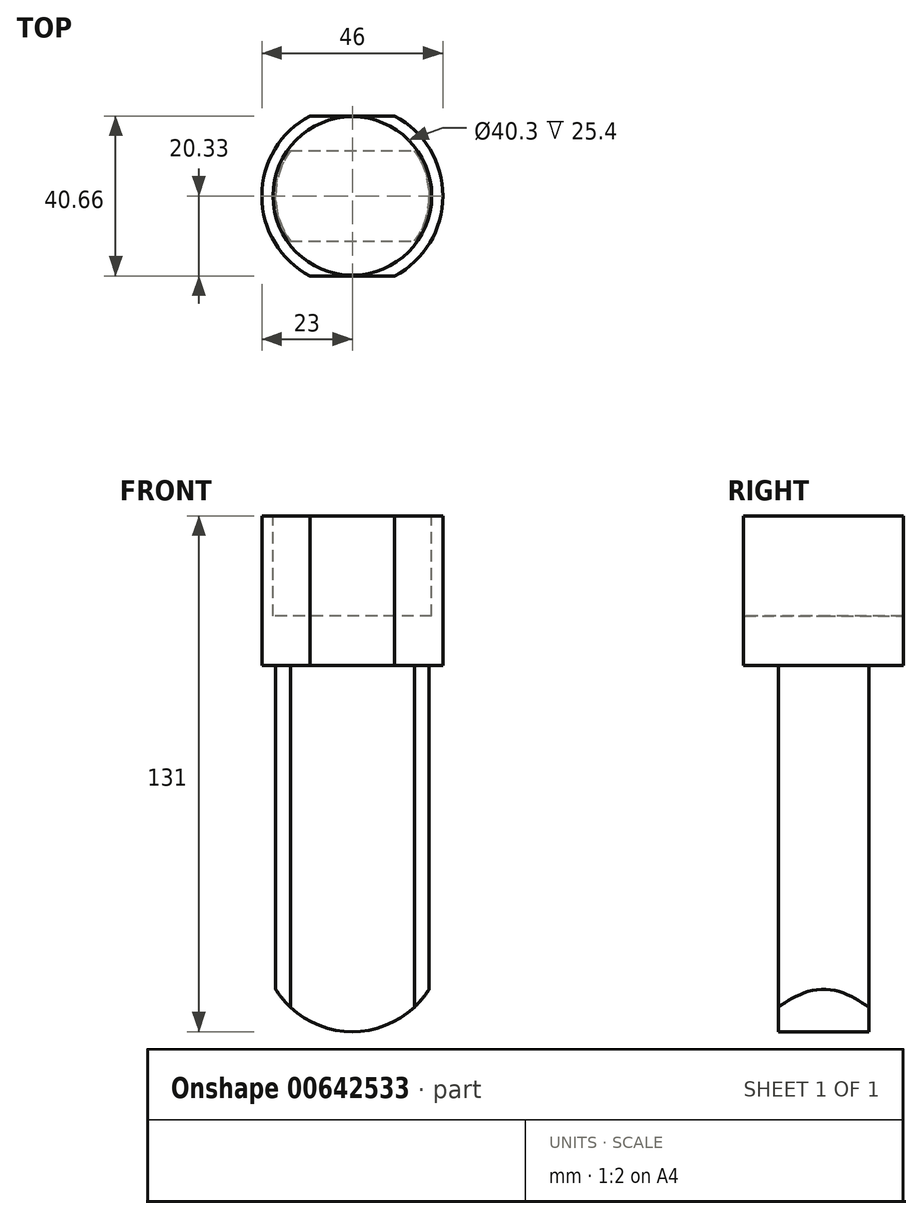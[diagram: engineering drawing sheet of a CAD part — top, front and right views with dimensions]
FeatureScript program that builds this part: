
annotation { "Feature Type Name" : "Feature", "Feature Type Description" : "" }
export const myFeature = defineFeature(function(context is Context, id is Id, definition is map)
    precondition{}
    {
        {
            var Q0;
            Q0=qCreatedBy(makeId("Top.planeOp"),FACE);
            var sketch = newSketch(context, id + "F0", { "sketchPlane" : qUnion([Q0])});
            skArc(sketch, "E0", {"start": v(-10.75, 20.33) * mm, "mid": v(-23, 0) * mm, "end": v(-10.75, -20.33) * mm});
            skLineSegment(sketch, "E1", {"start": v(-10.75, 20.33) * mm, "end": v(10.75, 20.33) * mm});
            skLineSegment(sketch, "E2.MirrorCS", {"start": v(-10.75, -20.33) * mm, "end": v(10.75, -20.33) * mm});
            skArc(sketch, "E3.trimOffspring", {"start": v(10.75, -20.33) * mm, "mid": v(23, 0) * mm, "end": v(10.75, 20.33) * mm});
            skSolve(sketch);
        }
        {
            var Q0;
            Q0=makeQuery(id+"F0.imprint","IMPRINT",FACE,{"disambiguationData":[TD([[makeQuery(id+"F0.imprint","IMPRINT",EDGE,{"derivedFrom":sQuery(id+"F0.wireOp",EDGE,"E0")}),1.0]])]});
            extrude(context, id + "F1", {"entities" : qUnion([Q0]), "depth" : 38 * mm, "offsetDistance" : 25.4 * mm});
        }
        {
            var Q0;
            Q0=makeQuery(id+"F1.opExtrude","CAP_FACE",FACE,{"disambiguationData":[OSD([sQuery(id+"F0.wireOp",EDGE,"E0"),sQuery(id+"F0.wireOp",EDGE,"E1"),sQuery(id+"F0.wireOp",EDGE,"E2.MirrorCS"),sQuery(id+"F0.wireOp",EDGE,"E3.trimOffspring")])],"isStart":false});
            var sketch = newSketch(context, id + "F2", { "sketchPlane" : qUnion([Q0])});
            skCircle(sketch, "E4", {"center": v(0, 0) * mm, "radius": 20.15 * mm});
            skSolve(sketch);
        }
        {
            var Q0;
            Q0 = qSketchRegion(id + "F2", true);
            extrude(context, id + "F3", {"entities" : qUnion([Q0]), "operationType" : NewBodyOperationType.REMOVE, "oppositeDirection" : true, "depth" : 25.4 * mm, "offsetDistance" : 25.4 * mm});
        }
        {
            var Q0;
            Q0=makeQuery(id+"F1.opExtrude","CAP_FACE",FACE,{"disambiguationData":[OSD([sQuery(id+"F0.wireOp",EDGE,"E0"),sQuery(id+"F0.wireOp",EDGE,"E1"),sQuery(id+"F0.wireOp",EDGE,"E2.MirrorCS"),sQuery(id+"F0.wireOp",EDGE,"E3.trimOffspring")])],"isStart":true});
            var sketch = newSketch(context, id + "F4", { "sketchPlane" : qUnion([Q0])});
            skArc(sketch, "E5", {"start": v(-15.75, 11.5) * mm, "mid": v(-19.5, 0) * mm, "end": v(-15.75, -11.5) * mm});
            skLineSegment(sketch, "E6", {"start": v(-15.75, 11.5) * mm, "end": v(15.75, 11.5) * mm});
            skLineSegment(sketch, "E7.MirrorCS", {"start": v(-15.75, -11.5) * mm, "end": v(15.75, -11.5) * mm});
            skArc(sketch, "E8.trimOffspring", {"start": v(15.75, -11.5) * mm, "mid": v(19.5, 0) * mm, "end": v(15.75, 11.5) * mm});
            skSolve(sketch);
        }
        {
            var Q0;
            Q0=makeQuery(id+"F4.imprint","IMPRINT",FACE,{"disambiguationData":[TD([[makeQuery(id+"F4.imprint","IMPRINT",EDGE,{"derivedFrom":sQuery(id+"F4.wireOp",EDGE,"E5")}),1.0]])]});
            extrude(context, id + "F5", {"entities" : qUnion([Q0]), "operationType" : NewBodyOperationType.ADD, "depth" : 93 * mm, "offsetDistance" : 25.4 * mm});
        }
        {
            var Q0;
            Q0=makeQuery(id+"F5.opExtrude","SWEPT_FACE",FACE,{"disambiguationData":[OSD([sQuery(id+"F4.wireOp",EDGE,"E6")])]});
            var sketch = newSketch(context, id + "F6", { "sketchPlane" : qUnion([Q0])});
            skArc(sketch, "E9", {"start": v(-22.12, -76.3) * mm, "mid": v(1.02, -92.98) * mm, "end": v(22.6, -74.3) * mm});
            skLineSegment(sketch, "E10", {"start": v(-22.12, -76.3) * mm, "end": v(-44.18, -110.5) * mm});
            skLineSegment(sketch, "E11", {"start": v(-44.18, -110.5) * mm, "end": v(51.09, -107.82) * mm});
            skLineSegment(sketch, "E12", {"start": v(51.09, -107.82) * mm, "end": v(22.6, -74.3) * mm});
            skSolve(sketch);
        }
        {
            var Q0;
            {var subQ0=sQuery(id+"F6.wireOp",EDGE,"E10");Q0=makeQuery(id+"F6.imprint","IMPRINT",FACE,{"disambiguationData":[TD([[makeQuery(id+"F6.imprint","IMPRINT",EDGE,{"derivedFrom":subQ0}),1.0]])]});}
            var Q1;
            {var subQ0=sQuery(id+"F6.wireOp",EDGE,"E9");var subQ1=sQuery(id+"F4.wireOp",EDGE,"E6");var subQ4=makeQuery(id+"F5.opExtrude","CAP_EDGE",EDGE,{"disambiguationData":[OSD([subQ1])],"isStart":false});var subQ5=makeQuery(id+"F6.imprint","INTERSECT",VERTEX,{"derivedFrom":[subQ4,subQ0]});Q1=makeQuery(id+"F6.imprint","IMPRINT",FACE,{"disambiguationData":[TD([[makeQuery(id+"F6.imprint","IMPRINT",EDGE,{"disambiguationData":[TD([[subQ5,1.0]])],"derivedFrom":subQ0}),-1.0]])]});}
            var Q2;
            {var subQ0=sQuery(id+"F6.wireOp",EDGE,"E9");var subQ1=sQuery(id+"F4.wireOp",EDGE,"E6");var subQ4=makeQuery(id+"F5.opExtrude","CAP_EDGE",EDGE,{"disambiguationData":[OSD([subQ1])],"isStart":false});var subQ5=makeQuery(id+"F6.imprint","INTERSECT",VERTEX,{"derivedFrom":[subQ4,subQ0]});Q2=makeQuery(id+"F6.imprint","IMPRINT",FACE,{"disambiguationData":[TD([[makeQuery(id+"F6.imprint","IMPRINT",EDGE,{"disambiguationData":[TD([[subQ5,-1.0]])],"derivedFrom":subQ0}),-1.0]])]});}
            extrude(context, id + "F7", {"entities" : qUnion([Q0, Q1, Q2]), "operationType" : NewBodyOperationType.REMOVE, "endBound" : BoundingType.THROUGH_ALL, "oppositeDirection" : true, "depth" : 25.4 * mm, "offsetDistance" : 25.4 * mm});
        }
    });
